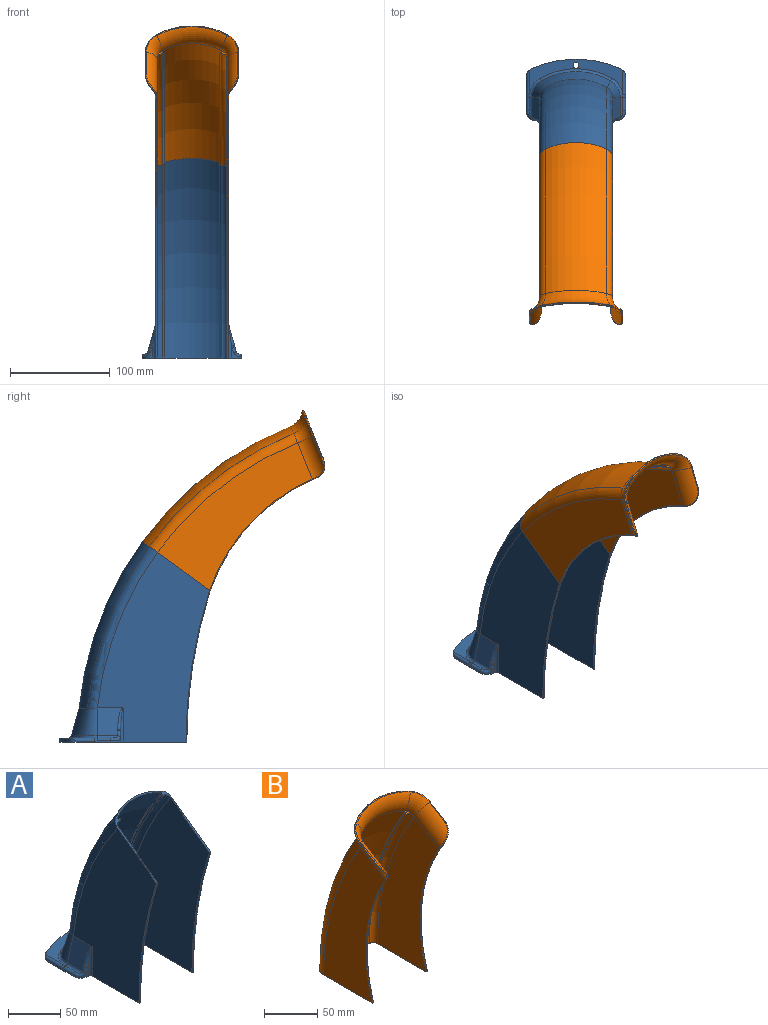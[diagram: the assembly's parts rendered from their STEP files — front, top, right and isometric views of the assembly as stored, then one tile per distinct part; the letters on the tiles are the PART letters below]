
ASSEMBLY  parts=2 mates=1
PART A: 59 faces, bbox 110x160.6x218.4 mm
  f0: plane 73.31x67.93mm, normal (0,-0.59,0.81), area 372.9mm2, adj f1,f8,f13,f14,f15,f16,f17,f18
  f1: plane 190.18x114.2mm, normal (-1,0,0), area 14553.2mm2, adj f0,f10,f15,f57
  f2: plane 11.96x0.4mm, normal (0,-1,0), area 4.5mm2, adj f10,f27,f39,f53
  f3: plane 33.62x1mm, normal (1,0,0), area 33.7mm2, adj f10,f11,f27,f48,f49,f50
  f4: cylinder r=111.8mm len=87.86mm, axis (0,0,-1), area 361.2mm2, adj f9,f10,f11,f12
  f5: plane 33.62x1mm, normal (-1,0,0), area 33.7mm2, adj f10,f12,f28,f41,f42,f43
  f6: plane 11.96x0.4mm, normal (0,-1,0), area 4.5mm2, adj f10,f28,f40,f46
  f7: cylinder r=3mm len=6mm, axis (0,0,-1), area 75.4mm2, adj f9,f10
  f8: plane 190.18x114.2mm, normal (1,0,0), area 14553.2mm2, adj f0,f10,f20,f58
  f9: plane 94.01x35.57mm, normal (0,0,1), area 1100.5mm2, adj f4,f7,f11,f12,f35,f36,f37,f41
  f10: plane 128.04x100mm, normal (0,0,-1), area 3286.4mm2, adj f1,f2,f3,f4,f5,f6,f7,f8
  f11: cylinder r=10mm len=9.2mm, axis (0,0,-1), area 37.5mm2, adj f3,f4,f9,f10,f48
  f12: cylinder r=10mm len=9.2mm, axis (0,0,-1), area 37.5mm2, adj f4,f5,f9,f10,f41
  f13: plane 190.38x112.6mm, normal (1,0,0), area 13615.9mm2, adj f0,f10,f16,f33,f39,f54,f57
  f14: plane 194.21x63.27mm, normal (-1,0,0), area 28.4mm2, adj f0,f10,f26,f56
  f15: torus R=323.3mm, axis (1,0,0), area 1764.1mm2, adj f0,f1,f10,f56
  f16: torus R=323.3mm, axis (1,0,0), area 2100.9mm2, adj f0,f13,f17,f32
  f17: torus R=280mm, axis (1,0,0), area 11553.8mm2, adj f0,f16,f18,f31
  f18: torus R=323.3mm, axis (1,0,0), area 2100.9mm2, adj f0,f17,f19,f30
  f19: plane 190.38x112.6mm, normal (-1,0,0), area 13615.9mm2, adj f0,f10,f18,f29,f40,f47,f58
  f20: torus R=323.3mm, axis (1,0,0), area 1764.1mm2, adj f0,f8,f10,f55
  f21: plane 194.21x63.27mm, normal (1,0,0), area 28.4mm2, adj f0,f10,f22,f55
  f22: cylinder r=330.16mm len=194.21mm, axis (1,0,0), area 415.3mm2, adj f0,f10,f21,f23
  f23: plane 195.27x64.96mm, normal (1,0,0), area 374.8mm2, adj f0,f10,f22,f24
  f24: torus R=280mm, axis (1,0,0), area 13327.7mm2, adj f0,f10,f23,f25
  f25: plane 195.27x64.96mm, normal (-1,0,0), area 374.8mm2, adj f0,f10,f24,f26
  f26: cylinder r=330.16mm len=194.21mm, axis (1,0,0), area 415.3mm2, adj f0,f10,f14,f25
  f27: cylinder r=10mm len=10.51mm, axis (0,0,-1), area 40.5mm2, adj f2,f3,f10,f51,f52
  f28: cylinder r=10mm len=10.51mm, axis (0,0,-1), area 40.5mm2, adj f5,f6,f10,f44,f45
  f29: plane 28.79x26.07mm, normal (-0.96,0,0.27), area 614mm2, adj f19,f30,f34,f45,f46,f47
  f30: bspline ~30.08x17.34mm, area 464.6mm2, adj f18,f29,f31,f35
  f31: bspline ~69.91x29.36mm, area 1932.5mm2, adj f17,f30,f32,f36
  f32: bspline ~30.08x17.34mm, area 464.6mm2, adj f16,f31,f33,f37
  f33: plane 28.79x26.07mm, normal (0.96,0,0.27), area 614mm2, adj f13,f32,f38,f52,f53,f54
  f34: cylinder r=3mm len=20.16mm, axis (0,-1,0), area 71.5mm2, adj f29,f35,f43,f44
  f35: bspline ~28.51x17.86mm, area 83.8mm2, adj f9,f30,f34,f36,f42
  f36: bspline ~109.05x22.93mm, area 287.1mm2, adj f9,f31,f35,f37
  f37: bspline ~28.49x17.85mm, area 83.8mm2, adj f9,f32,f36,f38,f49
  f38: cylinder r=3mm len=20.16mm, axis (0,1,0), area 71.5mm2, adj f33,f37,f50,f51
  f39: cylinder r=3mm len=33.68mm, axis (0,0,-1), area 121.5mm2, adj f2,f10,f13,f54
  f40: cylinder r=3mm len=33.68mm, axis (0,0,1), area 121.5mm2, adj f6,f10,f19,f47
  f41: cylinder r=3mm len=24.51mm, axis (0,1,0), area 98.7mm2, adj f5,f9,f12,f42
  f42: bspline ~7.37x3.3mm, area 13.7mm2, adj f5,f35,f41,f43
  f43: cylinder r=3mm len=13.3mm, axis (0,-1,0), area 61.4mm2, adj f5,f34,f42,f44
  f44: bspline ~10.12x8.19mm, area 49.1mm2, adj f28,f34,f43,f45
  f45: bspline ~10.61x6.04mm, area 23.9mm2, adj f28,f29,f44,f46
  f46: cylinder r=3mm len=3.29mm, axis (-0.27,0,-0.96), area 7.1mm2, adj f6,f29,f45,f47
  f47: bspline ~22.52x6mm, area 69.2mm2, adj f19,f29,f40,f46
  f48: cylinder r=3mm len=24.52mm, axis (0,-1,0), area 98.7mm2, adj f3,f9,f11,f49
  f49: bspline ~9.55x3.05mm, area 13.7mm2, adj f3,f37,f48,f50
  f50: cylinder r=3mm len=13.3mm, axis (0,1,0), area 61.4mm2, adj f3,f38,f49,f51
  f51: bspline ~10.95x8.19mm, area 49.1mm2, adj f27,f38,f50,f52
  f52: bspline ~10.61x6.04mm, area 23.9mm2, adj f27,f33,f51,f53
  f53: cylinder r=3mm len=3.29mm, axis (0.27,0,-0.96), area 7.1mm2, adj f2,f33,f52,f54
  f54: bspline ~22.52x6mm, area 69.2mm2, adj f13,f33,f39,f53
  f55: torus R=330.02mm, axis (1,0,0), area 466.8mm2, adj f0,f10,f20,f21
  f56: torus R=330.02mm, axis (-1,0,0), area 466.8mm2, adj f0,f10,f14,f15
  f57: torus R=500.8mm, axis (1,0,0), area 387.7mm2, adj f0,f1,f10,f13
  f58: torus R=500.8mm, axis (-1,0,0), area 387.7mm2, adj f0,f8,f10,f19
PART B: 57 faces, bbox 116.1x138.2x217 mm
  f0: plane 7.34x7mm, normal (0,-0.53,0.85), area 12.8mm2, adj f9,f10,f11,f12,f13,f28
  f1: plane 7.34x7mm, normal (0,-0.53,0.85), area 12.8mm2, adj f3,f4,f5,f6,f7,f24
  f2: plane 171.32x82.16mm, normal (1,0,0), area 8104.3mm2, adj f3,f20,f22,f55,f56
  f3: torus R=323.3mm, axis (1,0,0), area 1566.7mm2, adj f1,f2,f4,f20
  f4: torus R=330.02mm, axis (1,0,0), area 414.6mm2, adj f1,f3,f5,f20
  f5: plane 174.96x50.28mm, normal (1,0,0), area 25.2mm2, adj f1,f4,f6,f20
  f6: cylinder r=330.16mm len=174.96mm, axis (1,0,0), area 368.8mm2, adj f1,f5,f7,f20
  f7: plane 175.91x51.97mm, normal (1,0,0), area 332.8mm2, adj f1,f6,f8,f20
  f8: torus R=280mm, axis (1,0,0), area 11836.4mm2, adj f7,f9,f20,f26
  f9: plane 175.91x51.97mm, normal (-1,0,0), area 332.8mm2, adj f0,f8,f10,f20
  f10: cylinder r=330.16mm len=174.96mm, axis (1,0,0), area 368.8mm2, adj f0,f9,f11,f20
  f11: plane 174.96x50.28mm, normal (-1,0,0), area 25.2mm2, adj f0,f10,f12,f20
  f12: torus R=330.02mm, axis (1,0,0), area 414.6mm2, adj f0,f11,f13,f20
  f13: torus R=323.3mm, axis (1,0,0), area 1566.7mm2, adj f0,f12,f14,f20
  f14: plane 171.32x82.16mm, normal (-1,0,0), area 8104.2mm2, adj f13,f20,f30,f33,f35
  f15: plane 171.32x82.16mm, normal (1,0,0), area 8104.2mm2, adj f16,f20,f29,f31,f32
  f16: torus R=323.3mm, axis (1,0,0), area 2231mm2, adj f15,f17,f20,f27
  f17: torus R=280mm, axis (1,0,0), area 12207mm2, adj f16,f18,f20,f25
  f18: torus R=323.3mm, axis (1,0,0), area 2231mm2, adj f17,f19,f20,f23
  f19: plane 171.32x82.16mm, normal (-1,0,0), area 8104.2mm2, adj f18,f20,f21,f50,f53
  f20: plane 83.97x73.3mm, normal (0,0,-1), area 372.9mm2, adj f2,f3,f4,f5,f6,f7,f8,f9
  f21: cylinder r=18.87mm len=41.83mm, axis (0,0.85,0.53), area 734.6mm2, adj f19,f23,f46,f48,f51
  f22: cylinder r=20.47mm len=42.58mm, axis (0,0.85,0.53), area 796.9mm2, adj f2,f24,f49,f52,f54
  f23: torus R=30.47mm, axis (0,0.53,-0.85), area 319.9mm2, adj f18,f21,f25,f44
  f24: torus R=30.47mm, axis (0,0.53,-0.85), area 316.8mm2, adj f1,f22,f26,f47
  f25: torus R=80.47mm, axis (0,0.53,-0.85), area 1383.4mm2, adj f17,f23,f27,f42
  f26: torus R=80.47mm, axis (0,0.53,-0.85), area 1470.5mm2, adj f8,f24,f28,f45
  f27: torus R=30.47mm, axis (0,0.53,-0.85), area 319.9mm2, adj f16,f25,f29,f40
  f28: torus R=30.47mm, axis (0,0.53,-0.85), area 316.8mm2, adj f0,f26,f30,f43
  f29: cylinder r=18.87mm len=41.83mm, axis (0,-0.85,-0.53), area 734.6mm2, adj f15,f27,f34,f36,f38
  f30: cylinder r=20.47mm len=42.58mm, axis (0,-0.85,-0.53), area 796.9mm2, adj f14,f28,f37,f39,f41
  f31: torus R=190.8mm, axis (1,0,0), area 195.6mm2, adj f15,f20,f32,f33
  f32: cylinder r=0.8mm len=0.8mm, axis (0,0.53,-0.85), area 0mm2, adj f15,f31,f34
  f33: torus R=190.8mm, axis (-1,0,0), area 195.6mm2, adj f14,f20,f31,f35
  f34: torus R=19.67mm, axis (0,-0.85,-0.53), area 1.8mm2, adj f29,f32,f36,f37
  f35: cylinder r=0.8mm len=0.8mm, axis (0,-0.53,0.85), area 0mm2, adj f14,f33,f37
  f36: bspline ~24.55x11.64mm, area 33.4mm2, adj f29,f34,f38,f39
  f37: torus R=19.67mm, axis (0,-0.85,-0.53), area 1.9mm2, adj f30,f34,f35,f39
  f38: cylinder r=0.8mm len=19.85mm, axis (0,-0.85,-0.53), area 27.8mm2, adj f29,f36,f40,f41
  f39: bspline ~26.25x11.86mm, area 41.1mm2, adj f30,f36,f37,f41
  f40: torus R=21.14mm, axis (0,-0.53,0.85), area 28mm2, adj f27,f38,f42,f43
  f41: cylinder r=0.8mm len=19.53mm, axis (0,-0.85,-0.53), area 29.3mm2, adj f30,f38,f39,f43
  f42: torus R=71.14mm, axis (0,-0.53,0.85), area 92.1mm2, adj f25,f40,f44,f45
  f43: torus R=21.14mm, axis (0,-0.53,0.85), area 28.8mm2, adj f28,f40,f41,f45
  f44: torus R=21.14mm, axis (0,-0.53,0.85), area 28mm2, adj f23,f42,f46,f47
  f45: torus R=71.14mm, axis (0,-0.53,0.85), area 96.3mm2, adj f26,f42,f43,f47
  f46: cylinder r=0.8mm len=19.85mm, axis (0,0.85,0.53), area 27.8mm2, adj f21,f44,f48,f49
  f47: torus R=21.14mm, axis (0,-0.53,0.85), area 28.8mm2, adj f24,f44,f45,f49
  f48: bspline ~23.84x11.41mm, area 33.4mm2, adj f21,f46,f51,f52
  f49: cylinder r=0.8mm len=19.53mm, axis (0,0.85,0.53), area 29.3mm2, adj f22,f46,f47,f52
  f50: cylinder r=0.8mm len=0.8mm, axis (0,0.53,-0.85), area 0mm2, adj f19,f51,f53
  f51: torus R=19.67mm, axis (0,0.85,0.53), area 1.8mm2, adj f21,f48,f50,f54
  f52: bspline ~26.25x11.86mm, area 41.1mm2, adj f22,f48,f49,f54
  f53: torus R=190.8mm, axis (-1,0,0), area 195.6mm2, adj f19,f20,f50,f55
  f54: torus R=19.67mm, axis (0,0.85,0.53), area 1.9mm2, adj f22,f51,f52,f56
  f55: torus R=190.8mm, axis (1,0,0), area 195.6mm2, adj f2,f20,f53,f56
  f56: cylinder r=0.8mm len=0.8mm, axis (0,-0.53,0.85), area 0mm2, adj f2,f54,f55
PLACE A t=(0,-33.11,0)mm
PLACE B rot(axis=(1,0,0),36deg) t=(0,-90.16,175.41)mm
MATE fastened A.f0 <-> B.f20  axis (0,-0.59,0.81) through (0,-56.35,200)mm
